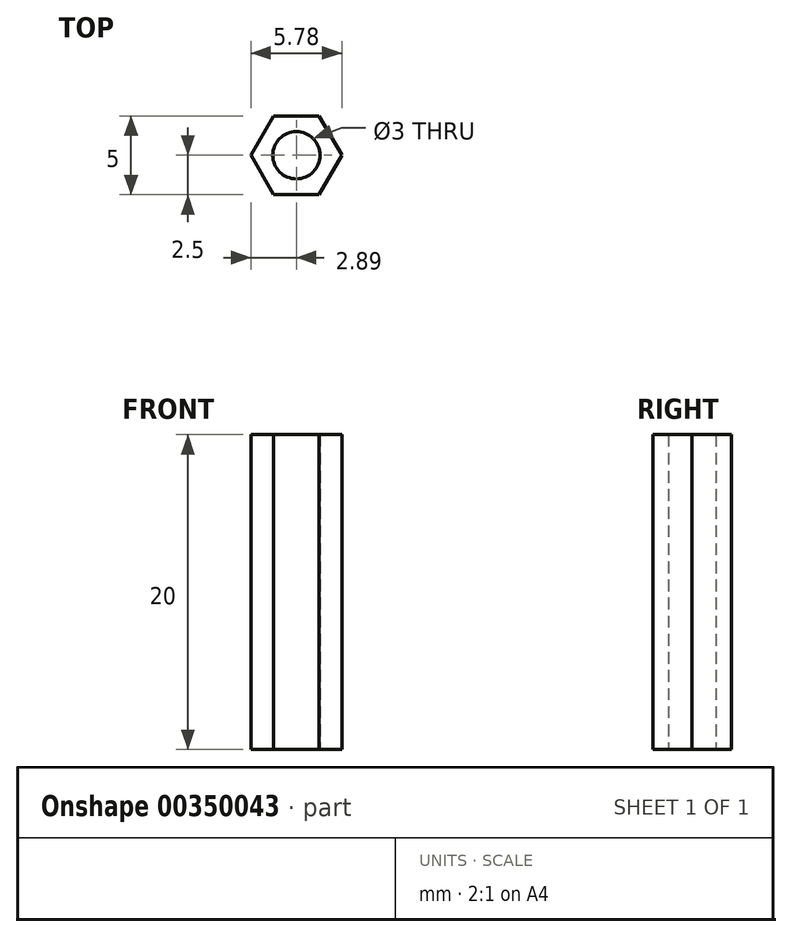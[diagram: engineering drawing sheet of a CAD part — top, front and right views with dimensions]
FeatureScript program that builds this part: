
annotation { "Feature Type Name" : "Feature", "Feature Type Description" : "" }
export const myFeature = defineFeature(function(context is Context, id is Id, definition is map)
    precondition{}
    {
        {
            var Q0;
            Q0=qCreatedBy(makeId("Top.planeOp"),FACE);
            var sketch = newSketch(context, id + "F0", { "sketchPlane" : qUnion([Q0])});
            skCircle(sketch, "E0", {"center": v(0, 0) * mm, "radius": 1.5 * mm});
            skCircle(sketch, "E1.cCircle", {"center": v(0, 0) * mm, "radius": 2.5 * mm, "construction": true});
            skLineSegment(sketch, "E1.0", {"start": v(-1.44, 2.5) * mm, "end": v(1.44, 2.5) * mm});
            skLineSegment(sketch, "E1.1", {"start": v(1.44, 2.5) * mm, "end": v(2.89, 0) * mm});
            skLineSegment(sketch, "E1.2", {"start": v(2.89, 0) * mm, "end": v(1.44, -2.5) * mm});
            skLineSegment(sketch, "E1.3", {"start": v(1.44, -2.5) * mm, "end": v(-1.44, -2.5) * mm});
            skLineSegment(sketch, "E1.4", {"start": v(-1.44, -2.5) * mm, "end": v(-2.89, 0) * mm});
            skLineSegment(sketch, "E1.5", {"start": v(-2.89, 0) * mm, "end": v(-1.44, 2.5) * mm});
            skPoint(sketch, "E1.0.midPoint", {"position": v(0, 2.5) * mm});
            skSolve(sketch);
        }
        {
            var Q0;
            Q0=qSketchRegion(id+"F0",true);
            extrude(context, id + "F1", {"entities" : qUnion([Q0]), "depth" : 20 * mm});
        }
    });
